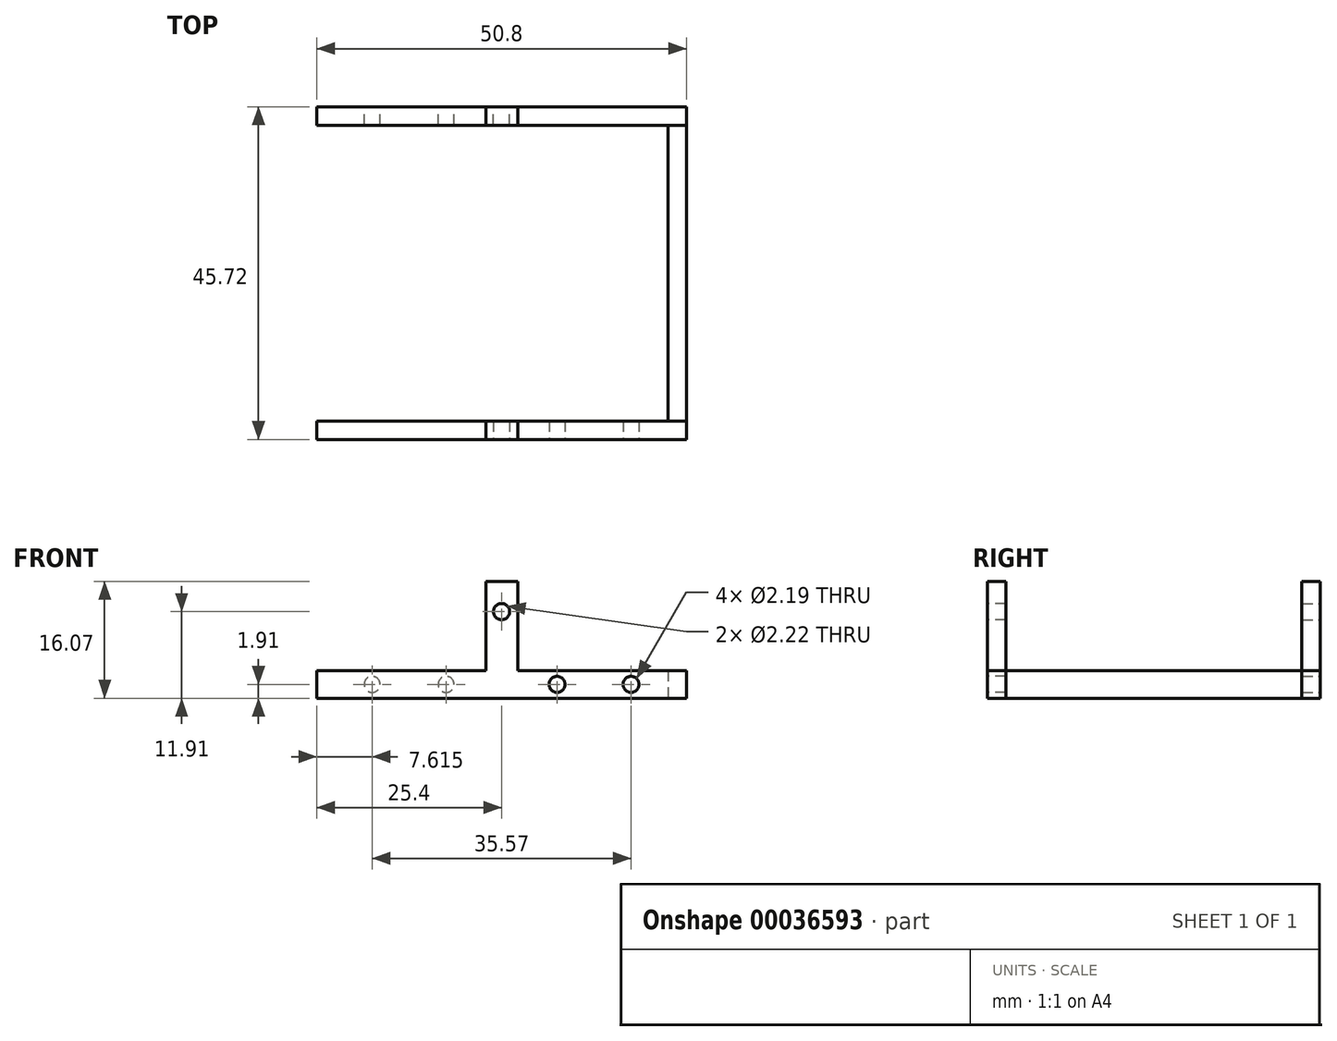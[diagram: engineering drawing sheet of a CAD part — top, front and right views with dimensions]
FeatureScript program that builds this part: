
annotation { "Feature Type Name" : "Feature", "Feature Type Description" : "" }
export const myFeature = defineFeature(function(context is Context, id is Id, definition is map)
    precondition{}
    {
        {
            var Q0;
            Q0=qCreatedBy(makeId("Front.planeOp"),FACE);
            var sketch = newSketch(context, id + "F0", { "sketchPlane" : qUnion([Q0])});
            skLineSegment(sketch, "E0.rect.bottom", {"start": v(25.4, 1.9) * mm, "end": v(-25.4, 1.9) * mm});
            skLineSegment(sketch, "E0.rect.top", {"start": v(25.4, -1.9) * mm, "end": v(-25.4, -1.9) * mm});
            skLineSegment(sketch, "E0.rect.left", {"start": v(25.4, 1.9) * mm, "end": v(25.4, -1.9) * mm});
            skLineSegment(sketch, "E0.rect.right", {"start": v(-25.4, 1.9) * mm, "end": v(-25.4, -1.9) * mm});
            skPoint(sketch, "E0.rect.middle", {"position": v(0, 0) * mm});
            skLineSegment(sketch, "E1.bottom", {"start": v(-2.16, -1.9) * mm, "end": v(2.2, -1.9) * mm});
            skLineSegment(sketch, "E1.top", {"start": v(-2.16, 14.16) * mm, "end": v(2.2, 14.16) * mm});
            skLineSegment(sketch, "E1.left", {"start": v(-2.16, -1.9) * mm, "end": v(-2.16, 14.16) * mm});
            skLineSegment(sketch, "E1.right", {"start": v(2.2, -1.9) * mm, "end": v(2.2, 14.16) * mm});
            skLineSegment(sketch, "E2", {"start": v(0.02, 14.16) * mm, "end": v(0.02, -1.9) * mm, "construction": true});
            skLineSegment(sketch, "E3", {"start": v(-2.16, 6.13) * mm, "end": v(0.02, 6.13) * mm, "construction": true});
            skLineSegment(sketch, "E4", {"start": v(0.02, 6.13) * mm, "end": v(2.2, 6.13) * mm, "construction": true});
            skSolve(sketch);
        }
        {
            var Q0;
            Q0 = qSketchRegion(id + "F0", true);
            extrude(context, id + "F1", {"entities" : qUnion([Q0]), "depth" : 2.54 * mm});
        }
        {
            var Q0;
            Q0=makeQuery(id+"F1.opExtrude","SWEPT_BODY",BODY,{"disambiguationData":[OSD([sQuery(id+"F0.wireOp",EDGE,"E0.rect.bottom"),sQuery(id+"F0.wireOp",EDGE,"E0.rect.top"),sQuery(id+"F0.wireOp",EDGE,"E0.rect.left"),sQuery(id+"F0.wireOp",EDGE,"E0.rect.right")])]});
            var Q1;
            Q1=makeQuery(id+"F1.opExtrude","SWEPT_EDGE",EDGE,{"disambiguationData":[OSD([sQuery(id+"F0.wireOp",EDGE,"E0.rect.bottom"),sQuery(id+"F0.wireOp",EDGE,"E0.rect.left")])]});
            var Q2;
            Q2=makeQuery(id+"F1.opExtrude","SWEPT_EDGE",EDGE,{"disambiguationData":[OSD([sQuery(id+"F0.wireOp",EDGE,"E0.rect.bottom"),sQuery(id+"F0.wireOp",EDGE,"E0.rect.right")])]});
            transform(context, id + "F2", {"entities" : qUnion([Q0]), "transformType" : TransformType.TRANSLATION_DISTANCE, "transformDirection" : qUnion([Q2]), "distance" : 20.32 * mm, "oppositeDirection" : true, "makeCopy" : false});
        }
        {
            var Q0;
            Q0=makeQuery(id+"F1.opExtrude","CAP_FACE",FACE,{"disambiguationData":[OSD([sQuery(id+"F0.wireOp",EDGE,"E0.rect.bottom"),sQuery(id+"F0.wireOp",EDGE,"E0.rect.top"),sQuery(id+"F0.wireOp",EDGE,"E0.rect.left"),sQuery(id+"F0.wireOp",EDGE,"E0.rect.right")])],"isStart":false});
            var sketch = newSketch(context, id + "F3", { "sketchPlane" : qUnion([Q0])});
            skLineSegment(sketch, "E5", {"start": v(7.62, 1.9) * mm, "end": v(7.62, -1.9) * mm, "construction": true});
            skLineSegment(sketch, "E6", {"start": v(17.79, 1.9) * mm, "end": v(17.79, -1.9) * mm, "construction": true});
            skCircle(sketch, "E7", {"center": v(7.62, 0) * mm, "radius": 1.1 * mm});
            skCircle(sketch, "E8", {"center": v(17.79, 0) * mm, "radius": 1.1 * mm});
            skLineSegment(sketch, "E9", {"start": v(7.62, 0) * mm, "end": v(17.79, 0) * mm, "construction": true});
            skPoint(sketch, "E10", {"position": v(12.7, 0) * mm});
            skLineSegment(sketch, "E11", {"start": v(12.7, 0) * mm, "end": v(12.7, -1.9) * mm, "construction": true});
            skLineSegment(sketch, "E12", {"start": v(0, 0) * mm, "end": v(0, -1.9) * mm, "construction": true});
            skLineSegment(sketch, "E13", {"start": v(0, -1.9) * mm, "end": v(25.4, -1.9) * mm, "construction": true});
            skLineSegment(sketch, "E14", {"start": v(0, 0) * mm, "end": v(0, 10) * mm, "construction": true});
            skCircle(sketch, "E15", {"center": v(0, 10) * mm, "radius": 1.11 * mm});
            skSolve(sketch);
        }
        {
            var Q0;
            Q0=makeQuery(id+"F1.opExtrude","SWEPT_BODY",BODY,{"disambiguationData":[OSD([sQuery(id+"F0.wireOp",EDGE,"E0.rect.bottom"),sQuery(id+"F0.wireOp",EDGE,"E0.rect.top"),sQuery(id+"F0.wireOp",EDGE,"E0.rect.left"),sQuery(id+"F0.wireOp",EDGE,"E0.rect.right")])]});
            var Q1;
            Q1=qCreatedBy(makeId("Front.planeOp"),FACE);
            mirror(context, id + "F4", {"entities" : qUnion([Q0]), "mirrorPlane" : qUnion([Q1])});
        }
        {
            var Q0;
            Q0 = qSketchRegion(id + "F3", true);
            extrude(context, id + "F5", {"entities" : qUnion([Q0]), "operationType" : NewBodyOperationType.REMOVE, "endBound" : BoundingType.UP_TO_NEXT, "oppositeDirection" : true, "depth" : 25.4 * mm});
        }
        {
            var Q0;
            Q0=makeQuery(id+"F1.opExtrude","SWEPT_FACE",FACE,{"disambiguationData":[OSD([sQuery(id+"F0.wireOp",EDGE,"E0.rect.left")])]});
            var sketch = newSketch(context, id + "F6", { "sketchPlane" : qUnion([Q0])});
            skLineSegment(sketch, "E16.0", {"start": v(-20.32, 1.9) * mm, "end": v(-20.32, -1.9) * mm});
            skLineSegment(sketch, "E17.bottom", {"start": v(-20.32, 1.9) * mm, "end": v(20.32, 1.9) * mm});
            skLineSegment(sketch, "E17.top", {"start": v(-20.32, -1.9) * mm, "end": v(20.32, -1.9) * mm});
            skLineSegment(sketch, "E17.right", {"start": v(20.32, 1.9) * mm, "end": v(20.32, -1.9) * mm});
            skSolve(sketch);
        }
        {
            var Q0;
            Q0 = qSketchRegion(id + "F6", true);
            extrude(context, id + "F7", {"entities" : qUnion([Q0]), "oppositeDirection" : true, "depth" : 2.54 * mm});
        }
        {
            var Q0;
            Q0=makeQuery(id+"F4.opPattern","COPY",FACE,{"derivedFrom":makeQuery(id+"F1.opExtrude","CAP_FACE",FACE,{"disambiguationData":[OSD([sQuery(id+"F0.wireOp",EDGE,"E0.rect.bottom"),sQuery(id+"F0.wireOp",EDGE,"E0.rect.top"),sQuery(id+"F0.wireOp",EDGE,"E0.rect.left"),sQuery(id+"F0.wireOp",EDGE,"E0.rect.right"),sQuery(id+"F0.wireOp",EDGE,"E1.bottom"),sQuery(id+"F0.wireOp",EDGE,"E1.top"),sQuery(id+"F0.wireOp",EDGE,"E1.left"),sQuery(id+"F0.wireOp",EDGE,"E1.right")])],"isStart":false}),"instanceName":"1"});
            var sketch = newSketch(context, id + "F8", { "sketchPlane" : qUnion([Q0])});
            skLineSegment(sketch, "E18", {"start": v(7.62, 1.9) * mm, "end": v(7.62, -1.9) * mm, "construction": true});
            skLineSegment(sketch, "E19", {"start": v(17.79, 1.9) * mm, "end": v(17.79, -1.9) * mm, "construction": true});
            skCircle(sketch, "E20", {"center": v(7.62, 0) * mm, "radius": 1.1 * mm});
            skCircle(sketch, "E21", {"center": v(17.79, 0) * mm, "radius": 1.1 * mm});
            skLineSegment(sketch, "E22", {"start": v(7.62, 0) * mm, "end": v(17.79, 0) * mm, "construction": true});
            skPoint(sketch, "E23", {"position": v(12.7, 0) * mm});
            skLineSegment(sketch, "E24", {"start": v(12.7, 0) * mm, "end": v(12.7, -1.9) * mm, "construction": true});
            skLineSegment(sketch, "E25", {"start": v(0, 0) * mm, "end": v(0, -1.9) * mm, "construction": true});
            skLineSegment(sketch, "E26", {"start": v(0, -1.9) * mm, "end": v(25.4, -1.9) * mm, "construction": true});
            skLineSegment(sketch, "E27", {"start": v(0, 0) * mm, "end": v(0, 10) * mm, "construction": true});
            skCircle(sketch, "E28", {"center": v(0, 10) * mm, "radius": 1.11 * mm});
            skSolve(sketch);
        }
        {
            var Q0;
            Q0 = qSketchRegion(id + "F8", true);
            extrude(context, id + "F9", {"entities" : qUnion([Q0]), "operationType" : NewBodyOperationType.REMOVE, "endBound" : BoundingType.UP_TO_NEXT, "oppositeDirection" : true, "depth" : 25.4 * mm});
        }
    });
